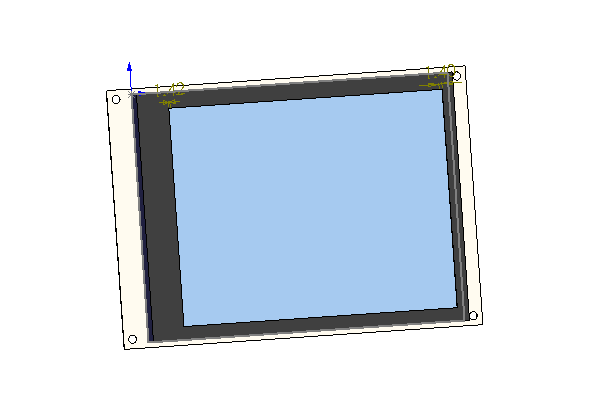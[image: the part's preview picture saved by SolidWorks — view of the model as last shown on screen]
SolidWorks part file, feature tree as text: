
SOLIDWORKS PART (.sldprt)
format: sldprt  version: not decoded by parser v0  size: 223,744 bytes
history: native  units: mm
features: sketch x4, extrude x2, cut_extrude x2, material x1 + 1 further entry (+12 scaffold rows collapsed)
feature tree (22):
  "Annotations"  RD1=1.404213mm RD2=1.424285mm
  scaffold x12  (default folders/planes/origin — collapsed)
  material  "Material <not specified>"
  sketch  "Sketch1"  dims[D1=141.0mm D2=104.7mm]
  extrude  "Extrude1"  Depth=6.2mm
  sketch  "Sketch4"  dims[D1=160.0mm D2=11.0mm D3=109.0mm D4=2.15mm]
  extrude  "Extrude2"  Depth=0.3mm
  sketch  "Sketch5"  dims[D2=3.5mm D3=3.5mm D4=3.5mm D5=3.5mm D1=101.0mm D6=4.0mm D7=4.0mm D8=152.0mm D9=~3.607962mm]
  cut_extrude  "Cut-Extrude1"  Depth=0.3mm
  sketch  "Sketch3"  dims[D1=122.0mm D2=92.0mm D3=~9.100403mm]
  cut_extrude  "Cut-Extrude4"  Depth=0.2mm
decode coverage: 8 of 8 modeling features carry decoded parameters; 1 rows unclassified (native names shown)
note: ~ marks probable driven/reference dimensions
note: suppression state not decoded; provenance and decode notes live in map.json
